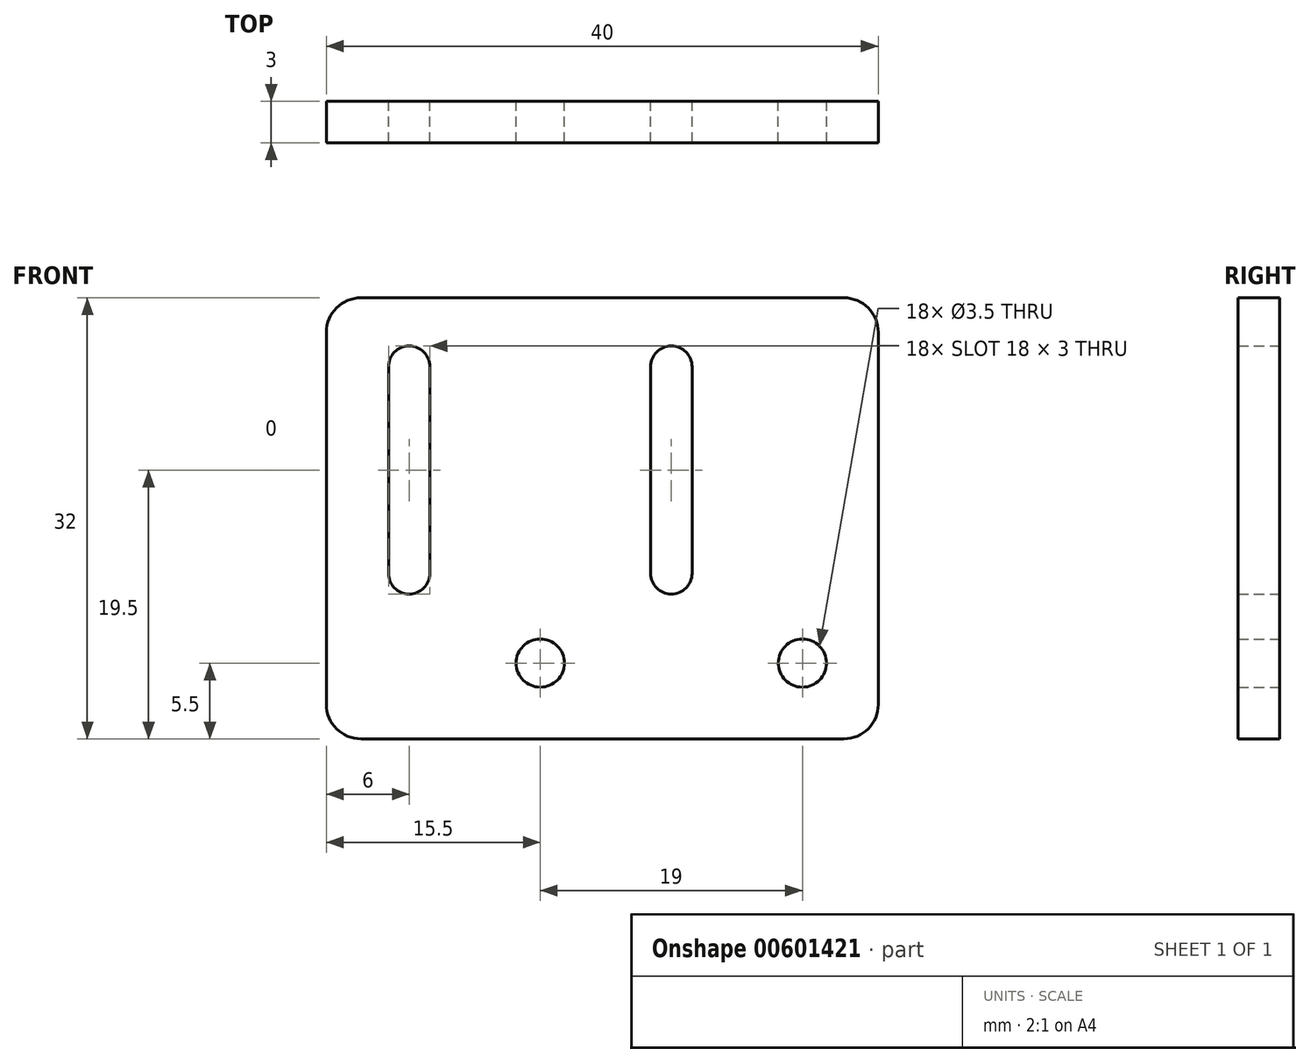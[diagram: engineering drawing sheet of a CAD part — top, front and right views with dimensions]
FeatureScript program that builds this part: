
annotation { "Feature Type Name" : "Feature", "Feature Type Description" : "" }
export const myFeature = defineFeature(function(context is Context, id is Id, definition is map)
    precondition{}
    {
        {
            var Q0;
            Q0=qCreatedBy(makeId("Front.planeOp"),FACE);
            var sketch = newSketch(context, id + "F0", { "sketchPlane" : qUnion([Q0])});
            skLineSegment(sketch, "E0", {"start": v(-9.5, 0) * mm, "end": v(9.5, 0) * mm, "construction": true});
            skCircle(sketch, "E1", {"center": v(-9.5, 0) * mm, "radius": 1.75 * mm});
            skCircle(sketch, "E2", {"center": v(9.5, 0) * mm, "radius": 1.75 * mm});
            skLineSegment(sketch, "E3", {"start": v(0, 6.5) * mm, "end": v(0, 21.5) * mm, "construction": true});
            skPoint(sketch, "E4.endSnap0", {"position": v(0, 14) * mm});
            skLineSegment(sketch, "E5", {"start": v(0, 14) * mm, "end": v(-19, 14) * mm, "construction": true});
            skLineSegment(sketch, "E6", {"start": v(-19, 21.5) * mm, "end": v(-19, 6.5) * mm, "construction": true});
            skArc(sketch, "E7.0.startCap", {"start": v(-20.5, 21.5) * mm, "mid": v(-19, 23) * mm, "end": v(-17.5, 21.5) * mm});
            skArc(sketch, "E7.0.endCap", {"start": v(-17.5, 6.5) * mm, "mid": v(-19, 5) * mm, "end": v(-20.5, 6.5) * mm});
            skLineSegment(sketch, "E7.0.left", {"start": v(-17.5, 21.5) * mm, "end": v(-17.5, 6.5) * mm});
            skLineSegment(sketch, "E7.0.right", {"start": v(-20.5, 21.5) * mm, "end": v(-20.5, 6.5) * mm});
            skArc(sketch, "E8.0.startCap", {"start": v(1.5, 6.5) * mm, "mid": v(0, 5) * mm, "end": v(-1.5, 6.5) * mm});
            skArc(sketch, "E8.0.endCap", {"start": v(-1.5, 21.5) * mm, "mid": v(0, 23) * mm, "end": v(1.5, 21.5) * mm});
            skLineSegment(sketch, "E8.0.left", {"start": v(-1.5, 6.5) * mm, "end": v(-1.5, 21.5) * mm});
            skLineSegment(sketch, "E8.0.right", {"start": v(1.5, 6.5) * mm, "end": v(1.5, 21.5) * mm});
            skLineSegment(sketch, "E9.bottom", {"start": v(12.5, -5.5) * mm, "end": v(-22.5, -5.5) * mm});
            skLineSegment(sketch, "E9.top", {"start": v(12.5, 26.5) * mm, "end": v(-22.5, 26.5) * mm});
            skLineSegment(sketch, "E9.left", {"start": v(15, -3) * mm, "end": v(15, 24) * mm});
            skLineSegment(sketch, "E9.right", {"start": v(-25, -3) * mm, "end": v(-25, 24) * mm});
            skPoint(sketch, "E9.middle", {"position": v(-5, 10.5) * mm});
            skPoint(sketch, "E10.visualSharp", {"position": v(-25, -5.5) * mm});
            skArc(sketch, "E10.filletArc", {"start": v(-25, -3) * mm, "mid": v(-24.27, -4.77) * mm, "end": v(-22.5, -5.5) * mm});
            skPoint(sketch, "E11.visualSharp", {"position": v(-25, 26.5) * mm});
            skArc(sketch, "E11.filletArc", {"start": v(-22.5, 26.5) * mm, "mid": v(-24.27, 25.77) * mm, "end": v(-25, 24) * mm});
            skPoint(sketch, "E12.visualSharp", {"position": v(15, 26.5) * mm});
            skArc(sketch, "E12.filletArc", {"start": v(15, 24) * mm, "mid": v(14.27, 25.77) * mm, "end": v(12.5, 26.5) * mm});
            skPoint(sketch, "E13.visualSharp", {"position": v(15, -5.5) * mm});
            skArc(sketch, "E13.filletArc", {"start": v(12.5, -5.5) * mm, "mid": v(14.27, -4.77) * mm, "end": v(15, -3) * mm});
            skSolve(sketch);
        }
        {
            var Q0;
            Q0 = qSketchRegion(id + "F0", true);
            extrude(context, id + "F1", {"entities" : qUnion([Q0]), "depth" : 3 * mm, "offsetDistance" : 25 * mm});
        }
    });
